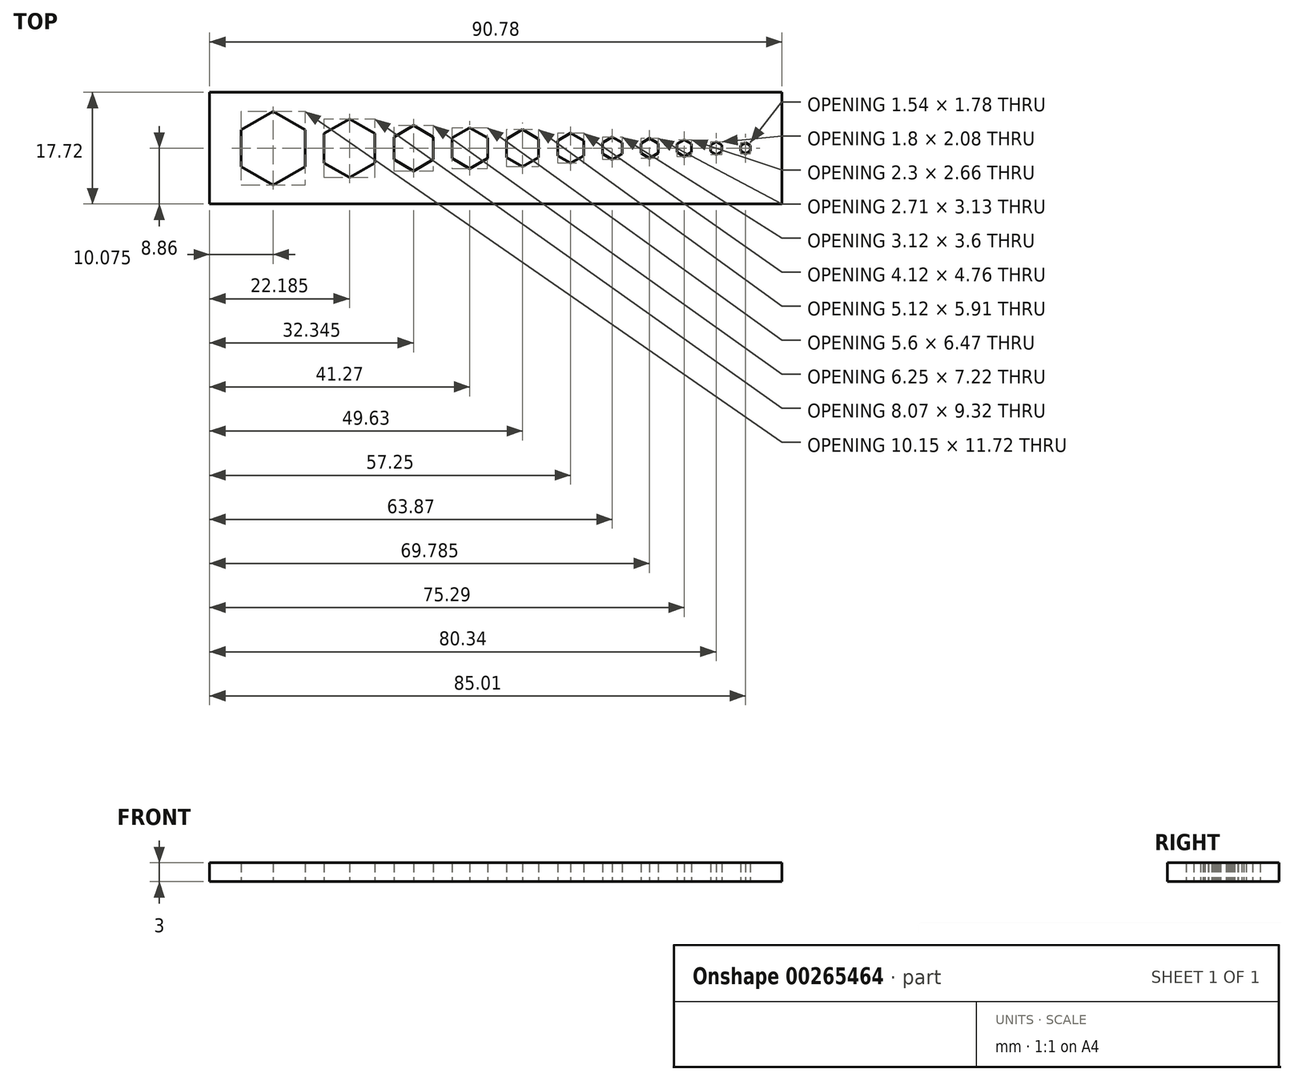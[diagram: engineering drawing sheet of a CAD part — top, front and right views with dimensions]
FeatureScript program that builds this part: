
annotation { "Feature Type Name" : "Feature", "Feature Type Description" : "" }
export const myFeature = defineFeature(function(context is Context, id is Id, definition is map)
    precondition{}
    {
        {
            var Q0;
            Q0=qCreatedBy(makeId("Top.planeOp"),FACE);
            var sketch = newSketch(context, id + "F0", { "sketchPlane" : qUnion([Q0])});
            skCircle(sketch, "E0.cCircle", {"center": v(-42.12, 0) * mm, "radius": 5.07 * mm, "construction": true});
            skLineSegment(sketch, "E0.0", {"start": v(-37.04, 2.93) * mm, "end": v(-37.04, -2.93) * mm});
            skLineSegment(sketch, "E0.1", {"start": v(-37.04, -2.93) * mm, "end": v(-42.12, -5.86) * mm});
            skLineSegment(sketch, "E0.2", {"start": v(-42.12, -5.86) * mm, "end": v(-47.2, -2.93) * mm});
            skLineSegment(sketch, "E0.3", {"start": v(-47.19, -2.93) * mm, "end": v(-47.19, 2.93) * mm});
            skLineSegment(sketch, "E0.4", {"start": v(-47.19, 2.93) * mm, "end": v(-42.11, 5.86) * mm});
            skLineSegment(sketch, "E0.5", {"start": v(-42.11, 5.86) * mm, "end": v(-37.04, 2.93) * mm});
            skPoint(sketch, "E0.0.midPoint", {"position": v(-37.04, 0) * mm});
            skCircle(sketch, "E1.cCircle", {"center": v(-30, 0) * mm, "radius": 4.03 * mm, "construction": true});
            skLineSegment(sketch, "E1.0", {"start": v(-25.97, 2.33) * mm, "end": v(-25.97, -2.33) * mm});
            skLineSegment(sketch, "E1.1", {"start": v(-25.97, -2.33) * mm, "end": v(-30, -4.66) * mm});
            skLineSegment(sketch, "E1.2", {"start": v(-30, -4.66) * mm, "end": v(-34.04, -2.33) * mm});
            skLineSegment(sketch, "E1.3", {"start": v(-34.04, -2.33) * mm, "end": v(-34.04, 2.33) * mm});
            skLineSegment(sketch, "E1.4", {"start": v(-34.04, 2.33) * mm, "end": v(-30, 4.66) * mm});
            skLineSegment(sketch, "E1.5", {"start": v(-30, 4.66) * mm, "end": v(-25.97, 2.33) * mm});
            skPoint(sketch, "E1.0.midPoint", {"position": v(-25.97, 0) * mm});
            skCircle(sketch, "E2.cCircle", {"center": v(-19.85, 0) * mm, "radius": 3.13 * mm, "construction": true});
            skLineSegment(sketch, "E2.0", {"start": v(-16.72, 1.8) * mm, "end": v(-16.72, -1.8) * mm});
            skLineSegment(sketch, "E2.1", {"start": v(-16.72, -1.8) * mm, "end": v(-19.84, -3.6) * mm});
            skLineSegment(sketch, "E2.2", {"start": v(-19.85, -3.6) * mm, "end": v(-22.97, -1.8) * mm});
            skLineSegment(sketch, "E2.3", {"start": v(-22.97, -1.8) * mm, "end": v(-22.97, 1.8) * mm});
            skLineSegment(sketch, "E2.4", {"start": v(-22.97, 1.8) * mm, "end": v(-19.84, 3.6) * mm});
            skLineSegment(sketch, "E2.5", {"start": v(-19.84, 3.6) * mm, "end": v(-16.72, 1.8) * mm});
            skPoint(sketch, "E2.0.midPoint", {"position": v(-16.72, 0) * mm});
            skCircle(sketch, "E3.cCircle", {"center": v(-10.92, 0) * mm, "radius": 2.8 * mm, "construction": true});
            skLineSegment(sketch, "E3.0", {"start": v(-8.12, 1.62) * mm, "end": v(-8.12, -1.62) * mm});
            skLineSegment(sketch, "E3.1", {"start": v(-8.12, -1.62) * mm, "end": v(-10.92, -3.23) * mm});
            skLineSegment(sketch, "E3.2", {"start": v(-10.92, -3.23) * mm, "end": v(-13.72, -1.62) * mm});
            skLineSegment(sketch, "E3.3", {"start": v(-13.72, -1.62) * mm, "end": v(-13.72, 1.62) * mm});
            skLineSegment(sketch, "E3.4", {"start": v(-13.72, 1.62) * mm, "end": v(-10.92, 3.23) * mm});
            skLineSegment(sketch, "E3.5", {"start": v(-10.92, 3.23) * mm, "end": v(-8.12, 1.62) * mm});
            skPoint(sketch, "E3.0.midPoint", {"position": v(-8.12, 0) * mm});
            skCircle(sketch, "E4.cCircle", {"center": v(-2.56, 0) * mm, "radius": 2.56 * mm, "construction": true});
            skLineSegment(sketch, "E4.0", {"start": v(0, 1.48) * mm, "end": v(0, -1.48) * mm});
            skLineSegment(sketch, "E4.1", {"start": v(0, -1.48) * mm, "end": v(-2.56, -2.96) * mm});
            skLineSegment(sketch, "E4.2", {"start": v(-2.56, -2.96) * mm, "end": v(-5.12, -1.48) * mm});
            skLineSegment(sketch, "E4.3", {"start": v(-5.12, -1.48) * mm, "end": v(-5.12, 1.48) * mm});
            skLineSegment(sketch, "E4.4", {"start": v(-5.12, 1.48) * mm, "end": v(-2.56, 2.96) * mm});
            skLineSegment(sketch, "E4.5", {"start": v(-2.56, 2.96) * mm, "end": v(0, 1.48) * mm});
            skPoint(sketch, "E4.0.midPoint", {"position": v(0, 0) * mm});
            skCircle(sketch, "E5.cCircle", {"center": v(5.06, 0) * mm, "radius": 2.06 * mm, "construction": true});
            skLineSegment(sketch, "E5.0", {"start": v(7.12, 1.19) * mm, "end": v(7.12, -1.19) * mm});
            skLineSegment(sketch, "E5.1", {"start": v(7.12, -1.19) * mm, "end": v(5.06, -2.38) * mm});
            skLineSegment(sketch, "E5.2", {"start": v(5.06, -2.38) * mm, "end": v(3, -1.19) * mm});
            skLineSegment(sketch, "E5.3", {"start": v(3, -1.19) * mm, "end": v(3, 1.19) * mm});
            skLineSegment(sketch, "E5.4", {"start": v(3, 1.19) * mm, "end": v(5.06, 2.38) * mm});
            skLineSegment(sketch, "E5.5", {"start": v(5.06, 2.38) * mm, "end": v(7.12, 1.19) * mm});
            skPoint(sketch, "E5.0.midPoint", {"position": v(7.12, 0) * mm});
            skCircle(sketch, "E6.cCircle", {"center": v(11.68, 0) * mm, "radius": 1.56 * mm, "construction": true});
            skLineSegment(sketch, "E6.0", {"start": v(13.24, 0.9) * mm, "end": v(13.24, -0.9) * mm});
            skLineSegment(sketch, "E6.1", {"start": v(13.24, -0.9) * mm, "end": v(11.68, -1.8) * mm});
            skLineSegment(sketch, "E6.2", {"start": v(11.68, -1.8) * mm, "end": v(10.12, -0.9) * mm});
            skLineSegment(sketch, "E6.3", {"start": v(10.12, -0.9) * mm, "end": v(10.12, 0.9) * mm});
            skLineSegment(sketch, "E6.4", {"start": v(10.12, 0.9) * mm, "end": v(11.68, 1.8) * mm});
            skLineSegment(sketch, "E6.5", {"start": v(11.68, 1.8) * mm, "end": v(13.24, 0.9) * mm});
            skPoint(sketch, "E6.0.midPoint", {"position": v(13.24, 0) * mm});
            skCircle(sketch, "E7.cCircle", {"center": v(17.6, 0) * mm, "radius": 1.35 * mm, "construction": true});
            skLineSegment(sketch, "E7.0", {"start": v(18.95, 0.78) * mm, "end": v(18.95, -0.78) * mm});
            skLineSegment(sketch, "E7.1", {"start": v(18.95, -0.78) * mm, "end": v(17.6, -1.56) * mm});
            skLineSegment(sketch, "E7.2", {"start": v(17.6, -1.56) * mm, "end": v(16.24, -0.78) * mm});
            skLineSegment(sketch, "E7.3", {"start": v(16.24, -0.78) * mm, "end": v(16.24, 0.78) * mm});
            skLineSegment(sketch, "E7.4", {"start": v(16.24, 0.78) * mm, "end": v(17.6, 1.56) * mm});
            skLineSegment(sketch, "E7.5", {"start": v(17.6, 1.56) * mm, "end": v(18.95, 0.78) * mm});
            skPoint(sketch, "E7.0.midPoint", {"position": v(18.95, 0) * mm});
            skCircle(sketch, "E8.cCircle", {"center": v(23.1, 0) * mm, "radius": 1.15 * mm, "construction": true});
            skLineSegment(sketch, "E8.0", {"start": v(24.25, 0.66) * mm, "end": v(24.25, -0.66) * mm});
            skLineSegment(sketch, "E8.1", {"start": v(24.25, -0.66) * mm, "end": v(23.1, -1.33) * mm});
            skLineSegment(sketch, "E8.2", {"start": v(23.1, -1.33) * mm, "end": v(21.95, -0.66) * mm});
            skLineSegment(sketch, "E8.3", {"start": v(21.95, -0.66) * mm, "end": v(21.95, 0.66) * mm});
            skLineSegment(sketch, "E8.4", {"start": v(21.95, 0.66) * mm, "end": v(23.1, 1.33) * mm});
            skLineSegment(sketch, "E8.5", {"start": v(23.1, 1.33) * mm, "end": v(24.25, 0.66) * mm});
            skPoint(sketch, "E8.0.midPoint", {"position": v(24.25, 0) * mm});
            skCircle(sketch, "E9.cCircle", {"center": v(28.15, 0) * mm, "radius": 0.9 * mm, "construction": true});
            skLineSegment(sketch, "E9.0", {"start": v(29.05, 0.52) * mm, "end": v(29.05, -0.52) * mm});
            skLineSegment(sketch, "E9.1", {"start": v(29.05, -0.52) * mm, "end": v(28.15, -1.04) * mm});
            skLineSegment(sketch, "E9.2", {"start": v(28.15, -1.04) * mm, "end": v(27.25, -0.52) * mm});
            skLineSegment(sketch, "E9.3", {"start": v(27.25, -0.52) * mm, "end": v(27.25, 0.52) * mm});
            skLineSegment(sketch, "E9.4", {"start": v(27.25, 0.52) * mm, "end": v(28.15, 1.04) * mm});
            skLineSegment(sketch, "E9.5", {"start": v(28.15, 1.04) * mm, "end": v(29.05, 0.52) * mm});
            skPoint(sketch, "E9.0.midPoint", {"position": v(29.05, 0) * mm});
            skCircle(sketch, "E10.cCircle", {"center": v(32.82, 0) * mm, "radius": 0.77 * mm, "construction": true});
            skLineSegment(sketch, "E10.0", {"start": v(33.6, 0.44) * mm, "end": v(33.6, -0.44) * mm});
            skLineSegment(sketch, "E10.1", {"start": v(33.6, -0.44) * mm, "end": v(32.82, -0.89) * mm});
            skLineSegment(sketch, "E10.2", {"start": v(32.82, -0.89) * mm, "end": v(32.05, -0.44) * mm});
            skLineSegment(sketch, "E10.3", {"start": v(32.05, -0.44) * mm, "end": v(32.05, 0.44) * mm});
            skLineSegment(sketch, "E10.4", {"start": v(32.05, 0.44) * mm, "end": v(32.82, 0.89) * mm});
            skLineSegment(sketch, "E10.5", {"start": v(32.82, 0.89) * mm, "end": v(33.6, 0.44) * mm});
            skPoint(sketch, "E10.0.midPoint", {"position": v(33.6, 0) * mm});
            skLineSegment(sketch, "E11.bottom", {"start": v(-52.19, 8.86) * mm, "end": v(38.59, 8.86) * mm});
            skLineSegment(sketch, "E11.top", {"start": v(-52.19, -8.86) * mm, "end": v(38.59, -8.86) * mm});
            skLineSegment(sketch, "E11.left", {"start": v(-52.19, 8.86) * mm, "end": v(-52.19, -8.86) * mm});
            skLineSegment(sketch, "E11.right", {"start": v(38.59, 8.86) * mm, "end": v(38.59, -8.86) * mm});
            skLineSegment(sketch, "E12.left", {"start": v(-52.19, 8.86) * mm, "end": v(-52.19, 8.86) * mm});
            skLineSegment(sketch, "E12.right", {"start": v(38.59, 8.86) * mm, "end": v(38.59, 8.86) * mm});
            skLineSegment(sketch, "E13.top", {"start": v(-52.19, 17.86) * mm, "end": v(38.59, 17.86) * mm});
            skLineSegment(sketch, "E13.left", {"start": v(-52.19, 8.86) * mm, "end": v(-52.19, 17.86) * mm});
            skLineSegment(sketch, "E13.right", {"start": v(38.59, 8.86) * mm, "end": v(38.59, 17.86) * mm});
            skPoint(sketch, "E14", {"position": v(-52.75, 13.36) * mm});
            skPoint(sketch, "E14.positionSnap0", {"position": v(-52.19, 13.36) * mm});
            skPoint(sketch, "E15", {"position": v(39.77, 13.36) * mm});
            skLineSegment(sketch, "E16", {"start": v(-52.75, 13.36) * mm, "end": v(-37.75, 13.36) * mm});
            skLineSegment(sketch, "E17", {"start": v(39.77, 13.36) * mm, "end": v(14.77, 13.36) * mm});
            skLineSegment(sketch, "E18", {"start": v(-19, 13.56) * mm, "end": v(6, 13.56) * mm});
            skSolve(sketch);
        }
        {
            var Q0;
            Q0=makeQuery(id+"F0.imprint","IMPRINT",FACE,{"disambiguationData":[TD([[makeQuery(id+"F0.imprint","IMPRINT",EDGE,{"derivedFrom":sQuery(id+"F0.wireOp",EDGE,"E11.bottom")}),1.0]])]});
            var Q1;
            Q1=makeQuery(id+"F0.imprint","IMPRINT",FACE,{"disambiguationData":[TD([[makeQuery(id+"F0.imprint","IMPRINT",EDGE,{"derivedFrom":sQuery(id+"F0.wireOp",EDGE,"E0.0")}),1.0]])]});
            extrude(context, id + "F1", {"entities" : qUnion([Q0, Q1]), "depth" : 3 * mm});
        }
        {
            var Q0;
            Q0=makeQuery(id+"F1.opExtrude","CAP_FACE",FACE,{"disambiguationData":[OSD([sQuery(id+"F0.wireOp",EDGE,"E0.0"),sQuery(id+"F0.wireOp",EDGE,"E0.1"),sQuery(id+"F0.wireOp",EDGE,"E0.2"),sQuery(id+"F0.wireOp",EDGE,"E0.3"),sQuery(id+"F0.wireOp",EDGE,"E0.4"),sQuery(id+"F0.wireOp",EDGE,"E0.5"),sQuery(id+"F0.wireOp",EDGE,"E1.0"),sQuery(id+"F0.wireOp",EDGE,"E1.1"),sQuery(id+"F0.wireOp",EDGE,"E1.2"),sQuery(id+"F0.wireOp",EDGE,"E1.3"),sQuery(id+"F0.wireOp",EDGE,"E1.4"),sQuery(id+"F0.wireOp",EDGE,"E1.5"),sQuery(id+"F0.wireOp",EDGE,"E2.0"),sQuery(id+"F0.wireOp",EDGE,"E2.1"),sQuery(id+"F0.wireOp",EDGE,"E2.2"),sQuery(id+"F0.wireOp",EDGE,"E2.3"),sQuery(id+"F0.wireOp",EDGE,"E2.4"),sQuery(id+"F0.wireOp",EDGE,"E2.5"),sQuery(id+"F0.wireOp",EDGE,"E3.0"),sQuery(id+"F0.wireOp",EDGE,"E3.1"),sQuery(id+"F0.wireOp",EDGE,"E3.2"),sQuery(id+"F0.wireOp",EDGE,"E3.3"),sQuery(id+"F0.wireOp",EDGE,"E3.4"),sQuery(id+"F0.wireOp",EDGE,"E3.5"),sQuery(id+"F0.wireOp",EDGE,"E4.0"),sQuery(id+"F0.wireOp",EDGE,"E4.1"),sQuery(id+"F0.wireOp",EDGE,"E4.2"),sQuery(id+"F0.wireOp",EDGE,"E4.3"),sQuery(id+"F0.wireOp",EDGE,"E4.4"),sQuery(id+"F0.wireOp",EDGE,"E4.5"),sQuery(id+"F0.wireOp",EDGE,"E5.0"),sQuery(id+"F0.wireOp",EDGE,"E5.1"),sQuery(id+"F0.wireOp",EDGE,"E5.2"),sQuery(id+"F0.wireOp",EDGE,"E5.3"),sQuery(id+"F0.wireOp",EDGE,"E5.4"),sQuery(id+"F0.wireOp",EDGE,"E5.5"),sQuery(id+"F0.wireOp",EDGE,"E6.0"),sQuery(id+"F0.wireOp",EDGE,"E6.1"),sQuery(id+"F0.wireOp",EDGE,"E6.2"),sQuery(id+"F0.wireOp",EDGE,"E6.3"),sQuery(id+"F0.wireOp",EDGE,"E6.4"),sQuery(id+"F0.wireOp",EDGE,"E6.5"),sQuery(id+"F0.wireOp",EDGE,"E7.0"),sQuery(id+"F0.wireOp",EDGE,"E7.1"),sQuery(id+"F0.wireOp",EDGE,"E7.2"),sQuery(id+"F0.wireOp",EDGE,"E7.3"),sQuery(id+"F0.wireOp",EDGE,"E7.4"),sQuery(id+"F0.wireOp",EDGE,"E7.5"),sQuery(id+"F0.wireOp",EDGE,"E8.0"),sQuery(id+"F0.wireOp",EDGE,"E8.1"),sQuery(id+"F0.wireOp",EDGE,"E8.2"),sQuery(id+"F0.wireOp",EDGE,"E8.3"),sQuery(id+"F0.wireOp",EDGE,"E8.4"),sQuery(id+"F0.wireOp",EDGE,"E8.5"),sQuery(id+"F0.wireOp",EDGE,"E9.0"),sQuery(id+"F0.wireOp",EDGE,"E9.1"),sQuery(id+"F0.wireOp",EDGE,"E9.2"),sQuery(id+"F0.wireOp",EDGE,"E9.3"),sQuery(id+"F0.wireOp",EDGE,"E9.4"),sQuery(id+"F0.wireOp",EDGE,"E9.5"),sQuery(id+"F0.wireOp",EDGE,"E10.0"),sQuery(id+"F0.wireOp",EDGE,"E10.1"),sQuery(id+"F0.wireOp",EDGE,"E10.2"),sQuery(id+"F0.wireOp",EDGE,"E10.3"),sQuery(id+"F0.wireOp",EDGE,"E10.4"),sQuery(id+"F0.wireOp",EDGE,"E10.5"),sQuery(id+"F0.wireOp",EDGE,"E11.top"),sQuery(id+"F0.wireOp",EDGE,"E11.left"),sQuery(id+"F0.wireOp",EDGE,"E11.right"),sQuery(id+"F0.wireOp",EDGE,"E13.top"),sQuery(id+"F0.wireOp",EDGE,"E13.left"),sQuery(id+"F0.wireOp",EDGE,"E13.right")])],"isStart":false});
            var sketch = newSketch(context, id + "F2", { "sketchPlane" : qUnion([Q0])});
            skPoint(sketch, "E19", {"position": v(33.59, 13.5) * mm});
            skPoint(sketch, "E20", {"position": v(15.59, 13.5) * mm});
            skPoint(sketch, "E21", {"position": v(2.2, 13.5) * mm});
            skPoint(sketch, "E22", {"position": v(-15.8, 13.5) * mm});
            skPoint(sketch, "E23", {"position": v(-29.19, 13.5) * mm});
            skPoint(sketch, "E24", {"position": v(-47.19, 13.5) * mm});
            skSolve(sketch);
        }
        {
            var Q0;
            Q0=sQuery(id+"F2.wireOp",VERTEX,"E24");
            var Q1;
            Q1=sQuery(id+"F2.wireOp",VERTEX,"E23");
            var Q2;
            Q2=sQuery(id+"F2.wireOp",VERTEX,"E22");
            var Q3;
            Q3=sQuery(id+"F2.wireOp",VERTEX,"E21");
            var Q4;
            Q4=sQuery(id+"F2.wireOp",VERTEX,"E20");
            var Q5;
            Q5=sQuery(id+"F2.wireOp",VERTEX,"E19");
            var Q6;
            Q6=makeQuery(id+"F1.opExtrude","SWEPT_BODY",BODY,{"disambiguationData":[OSD([sQuery(id+"F0.wireOp",EDGE,"E0.0"),sQuery(id+"F0.wireOp",EDGE,"E0.1"),sQuery(id+"F0.wireOp",EDGE,"E0.2"),sQuery(id+"F0.wireOp",EDGE,"E0.3"),sQuery(id+"F0.wireOp",EDGE,"E0.4"),sQuery(id+"F0.wireOp",EDGE,"E0.5"),sQuery(id+"F0.wireOp",EDGE,"E1.0"),sQuery(id+"F0.wireOp",EDGE,"E1.1"),sQuery(id+"F0.wireOp",EDGE,"E1.2"),sQuery(id+"F0.wireOp",EDGE,"E1.3"),sQuery(id+"F0.wireOp",EDGE,"E1.4"),sQuery(id+"F0.wireOp",EDGE,"E1.5"),sQuery(id+"F0.wireOp",EDGE,"E2.0"),sQuery(id+"F0.wireOp",EDGE,"E2.1"),sQuery(id+"F0.wireOp",EDGE,"E2.2"),sQuery(id+"F0.wireOp",EDGE,"E2.3"),sQuery(id+"F0.wireOp",EDGE,"E2.4"),sQuery(id+"F0.wireOp",EDGE,"E2.5"),sQuery(id+"F0.wireOp",EDGE,"E3.0"),sQuery(id+"F0.wireOp",EDGE,"E3.1"),sQuery(id+"F0.wireOp",EDGE,"E3.2"),sQuery(id+"F0.wireOp",EDGE,"E3.3"),sQuery(id+"F0.wireOp",EDGE,"E3.4"),sQuery(id+"F0.wireOp",EDGE,"E3.5"),sQuery(id+"F0.wireOp",EDGE,"E4.0"),sQuery(id+"F0.wireOp",EDGE,"E4.1"),sQuery(id+"F0.wireOp",EDGE,"E4.2"),sQuery(id+"F0.wireOp",EDGE,"E4.3"),sQuery(id+"F0.wireOp",EDGE,"E4.4"),sQuery(id+"F0.wireOp",EDGE,"E4.5"),sQuery(id+"F0.wireOp",EDGE,"E5.0"),sQuery(id+"F0.wireOp",EDGE,"E5.1"),sQuery(id+"F0.wireOp",EDGE,"E5.2"),sQuery(id+"F0.wireOp",EDGE,"E5.3"),sQuery(id+"F0.wireOp",EDGE,"E5.4"),sQuery(id+"F0.wireOp",EDGE,"E5.5"),sQuery(id+"F0.wireOp",EDGE,"E6.0"),sQuery(id+"F0.wireOp",EDGE,"E6.1"),sQuery(id+"F0.wireOp",EDGE,"E6.2"),sQuery(id+"F0.wireOp",EDGE,"E6.3"),sQuery(id+"F0.wireOp",EDGE,"E6.4"),sQuery(id+"F0.wireOp",EDGE,"E6.5"),sQuery(id+"F0.wireOp",EDGE,"E7.0"),sQuery(id+"F0.wireOp",EDGE,"E7.1"),sQuery(id+"F0.wireOp",EDGE,"E7.2"),sQuery(id+"F0.wireOp",EDGE,"E7.3"),sQuery(id+"F0.wireOp",EDGE,"E7.4"),sQuery(id+"F0.wireOp",EDGE,"E7.5"),sQuery(id+"F0.wireOp",EDGE,"E8.0"),sQuery(id+"F0.wireOp",EDGE,"E8.1"),sQuery(id+"F0.wireOp",EDGE,"E8.2"),sQuery(id+"F0.wireOp",EDGE,"E8.3"),sQuery(id+"F0.wireOp",EDGE,"E8.4"),sQuery(id+"F0.wireOp",EDGE,"E8.5"),sQuery(id+"F0.wireOp",EDGE,"E9.0"),sQuery(id+"F0.wireOp",EDGE,"E9.1"),sQuery(id+"F0.wireOp",EDGE,"E9.2"),sQuery(id+"F0.wireOp",EDGE,"E9.3"),sQuery(id+"F0.wireOp",EDGE,"E9.4"),sQuery(id+"F0.wireOp",EDGE,"E9.5"),sQuery(id+"F0.wireOp",EDGE,"E10.0"),sQuery(id+"F0.wireOp",EDGE,"E10.1"),sQuery(id+"F0.wireOp",EDGE,"E10.2"),sQuery(id+"F0.wireOp",EDGE,"E10.3"),sQuery(id+"F0.wireOp",EDGE,"E10.4"),sQuery(id+"F0.wireOp",EDGE,"E10.5"),sQuery(id+"F0.wireOp",EDGE,"E11.top"),sQuery(id+"F0.wireOp",EDGE,"E11.left"),sQuery(id+"F0.wireOp",EDGE,"E11.right"),sQuery(id+"F0.wireOp",EDGE,"E13.top"),sQuery(id+"F0.wireOp",EDGE,"E13.left"),sQuery(id+"F0.wireOp",EDGE,"E13.right")])]});
            hole(context, id + "F3", {"style" : HoleStyle.SIMPLE, "endStyle" : HoleEndStyle.THROUGH, "standardTappedOrClearance" : lookupTablePath({ "standard" : "ISO", "fit" : "Normal", "size" : "M6", "type" : "Clearance" }), "standardBlindInLast" : lookupTablePath({ "fit" : "Standard", "standard" : "ISO", "size" : "M6", "type" : "Clearance" }), "holeDiameter" : 6.6 * mm, "tappedDepth" : 12 * mm, "tapClearance" : 3, "locations" : qUnion([Q0, Q1, Q2, Q3, Q4, Q5]), "scope" : qUnion([Q6])});
        }
        {
            var Q0;
            Q0=makeQuery(id+"F1.opExtrude","CAP_FACE",FACE,{"disambiguationData":[OSD([sQuery(id+"F0.wireOp",EDGE,"E0.0"),sQuery(id+"F0.wireOp",EDGE,"E0.1"),sQuery(id+"F0.wireOp",EDGE,"E0.2"),sQuery(id+"F0.wireOp",EDGE,"E0.3"),sQuery(id+"F0.wireOp",EDGE,"E0.4"),sQuery(id+"F0.wireOp",EDGE,"E0.5"),sQuery(id+"F0.wireOp",EDGE,"E1.0"),sQuery(id+"F0.wireOp",EDGE,"E1.1"),sQuery(id+"F0.wireOp",EDGE,"E1.2"),sQuery(id+"F0.wireOp",EDGE,"E1.3"),sQuery(id+"F0.wireOp",EDGE,"E1.4"),sQuery(id+"F0.wireOp",EDGE,"E1.5"),sQuery(id+"F0.wireOp",EDGE,"E2.0"),sQuery(id+"F0.wireOp",EDGE,"E2.1"),sQuery(id+"F0.wireOp",EDGE,"E2.2"),sQuery(id+"F0.wireOp",EDGE,"E2.3"),sQuery(id+"F0.wireOp",EDGE,"E2.4"),sQuery(id+"F0.wireOp",EDGE,"E2.5"),sQuery(id+"F0.wireOp",EDGE,"E3.0"),sQuery(id+"F0.wireOp",EDGE,"E3.1"),sQuery(id+"F0.wireOp",EDGE,"E3.2"),sQuery(id+"F0.wireOp",EDGE,"E3.3"),sQuery(id+"F0.wireOp",EDGE,"E3.4"),sQuery(id+"F0.wireOp",EDGE,"E3.5"),sQuery(id+"F0.wireOp",EDGE,"E4.0"),sQuery(id+"F0.wireOp",EDGE,"E4.1"),sQuery(id+"F0.wireOp",EDGE,"E4.2"),sQuery(id+"F0.wireOp",EDGE,"E4.3"),sQuery(id+"F0.wireOp",EDGE,"E4.4"),sQuery(id+"F0.wireOp",EDGE,"E4.5"),sQuery(id+"F0.wireOp",EDGE,"E5.0"),sQuery(id+"F0.wireOp",EDGE,"E5.1"),sQuery(id+"F0.wireOp",EDGE,"E5.2"),sQuery(id+"F0.wireOp",EDGE,"E5.3"),sQuery(id+"F0.wireOp",EDGE,"E5.4"),sQuery(id+"F0.wireOp",EDGE,"E5.5"),sQuery(id+"F0.wireOp",EDGE,"E6.0"),sQuery(id+"F0.wireOp",EDGE,"E6.1"),sQuery(id+"F0.wireOp",EDGE,"E6.2"),sQuery(id+"F0.wireOp",EDGE,"E6.3"),sQuery(id+"F0.wireOp",EDGE,"E6.4"),sQuery(id+"F0.wireOp",EDGE,"E6.5"),sQuery(id+"F0.wireOp",EDGE,"E7.0"),sQuery(id+"F0.wireOp",EDGE,"E7.1"),sQuery(id+"F0.wireOp",EDGE,"E7.2"),sQuery(id+"F0.wireOp",EDGE,"E7.3"),sQuery(id+"F0.wireOp",EDGE,"E7.4"),sQuery(id+"F0.wireOp",EDGE,"E7.5"),sQuery(id+"F0.wireOp",EDGE,"E8.0"),sQuery(id+"F0.wireOp",EDGE,"E8.1"),sQuery(id+"F0.wireOp",EDGE,"E8.2"),sQuery(id+"F0.wireOp",EDGE,"E8.3"),sQuery(id+"F0.wireOp",EDGE,"E8.4"),sQuery(id+"F0.wireOp",EDGE,"E8.5"),sQuery(id+"F0.wireOp",EDGE,"E9.0"),sQuery(id+"F0.wireOp",EDGE,"E9.1"),sQuery(id+"F0.wireOp",EDGE,"E9.2"),sQuery(id+"F0.wireOp",EDGE,"E9.3"),sQuery(id+"F0.wireOp",EDGE,"E9.4"),sQuery(id+"F0.wireOp",EDGE,"E9.5"),sQuery(id+"F0.wireOp",EDGE,"E10.0"),sQuery(id+"F0.wireOp",EDGE,"E10.1"),sQuery(id+"F0.wireOp",EDGE,"E10.2"),sQuery(id+"F0.wireOp",EDGE,"E10.3"),sQuery(id+"F0.wireOp",EDGE,"E10.4"),sQuery(id+"F0.wireOp",EDGE,"E10.5"),sQuery(id+"F0.wireOp",EDGE,"E11.top"),sQuery(id+"F0.wireOp",EDGE,"E11.left"),sQuery(id+"F0.wireOp",EDGE,"E11.right"),sQuery(id+"F0.wireOp",EDGE,"E13.top"),sQuery(id+"F0.wireOp",EDGE,"E13.left"),sQuery(id+"F0.wireOp",EDGE,"E13.right")])],"isStart":false});
            var sketch = newSketch(context, id + "F4", { "sketchPlane" : qUnion([Q0])});
            skLineSegment(sketch, "E25", {"start": v(-47.27, 16.8) * mm, "end": v(-29.2, 16.8) * mm});
            skLineSegment(sketch, "E26", {"start": v(-29.2, 16.8) * mm, "end": v(-29.2, 10.2) * mm});
            skLineSegment(sketch, "E27", {"start": v(-29.2, 10.2) * mm, "end": v(-47.1, 10.2) * mm});
            skLineSegment(sketch, "E28", {"start": v(-47.1, 10.2) * mm, "end": v(-47.27, 16.8) * mm});
            skLineSegment(sketch, "E29", {"start": v(-15.88, 16.8) * mm, "end": v(-15.88, 10.2) * mm});
            skLineSegment(sketch, "E30", {"start": v(-15.88, 10.2) * mm, "end": v(2.2, 10.2) * mm});
            skLineSegment(sketch, "E31", {"start": v(2.2, 10.2) * mm, "end": v(2.2, 16.8) * mm});
            skLineSegment(sketch, "E32", {"start": v(2.2, 16.8) * mm, "end": v(-15.88, 16.8) * mm});
            skLineSegment(sketch, "E33", {"start": v(15.5, 16.8) * mm, "end": v(15.5, 10.2) * mm});
            skLineSegment(sketch, "E34", {"start": v(15.5, 10.2) * mm, "end": v(33.7, 10.2) * mm});
            skLineSegment(sketch, "E35", {"start": v(33.7, 10.2) * mm, "end": v(33.7, 16.8) * mm});
            skLineSegment(sketch, "E36", {"start": v(33.7, 16.8) * mm, "end": v(15.5, 16.8) * mm});
            skSolve(sketch);
        }
        {
            var Q0;
            {var subQ6=sQuery(id+"F4.wireOp",EDGE,"E27");Q0=makeQuery(id+"F4.imprint","IMPRINT",FACE,{"disambiguationData":[TD([[makeQuery(id+"F4.imprint","IMPRINT",EDGE,{"derivedFrom":subQ6}),-1.0]])]});}
            var Q1;
            {var subQ1=sQuery(id+"F4.wireOp",EDGE,"E30");var subQ4=makeQuery(id+"F3.hole-2.boolean.opBoolean","COPY",EDGE,{"derivedFrom":makeQuery(id+"F3.hole-2.opRevolve","SWEPT_EDGE",EDGE,{"disambiguationData":[OSD([sQuery(id+"F3.hole-2.sketch.wireOp",EDGE,"core_line_2"),sQuery(id+"F3.hole-2.sketch.wireOp",EDGE,"core_line_3")])]})});var subQ5=makeQuery(id+"F4.imprint","INTERSECT",VERTEX,{"derivedFrom":[subQ4,subQ1]});Q1=makeQuery(id+"F4.imprint","IMPRINT",FACE,{"disambiguationData":[TD([[makeQuery(id+"F4.imprint","IMPRINT",EDGE,{"disambiguationData":[TD([[subQ5,-1.0]])],"derivedFrom":subQ1}),1.0]])]});}
            var Q2;
            {var subQ0=sQuery(id+"F4.wireOp",EDGE,"E34");var subQ1=makeQuery(id+"F3.hole-4.boolean.opBoolean","COPY",EDGE,{"derivedFrom":makeQuery(id+"F3.hole-4.opRevolve","SWEPT_EDGE",EDGE,{"disambiguationData":[OSD([sQuery(id+"F3.hole-4.sketch.wireOp",EDGE,"core_line_2"),sQuery(id+"F3.hole-4.sketch.wireOp",EDGE,"core_line_3")])]})});var subQ2=makeQuery(id+"F4.imprint","INTERSECT",VERTEX,{"derivedFrom":[subQ1,subQ0]});Q2=makeQuery(id+"F4.imprint","IMPRINT",FACE,{"disambiguationData":[TD([[makeQuery(id+"F4.imprint","IMPRINT",EDGE,{"disambiguationData":[TD([[subQ2,-1.0]])],"derivedFrom":subQ0}),1.0]])]});}
            extrude(context, id + "F5", {"entities" : qUnion([Q0, Q1, Q2]), "operationType" : NewBodyOperationType.REMOVE, "oppositeDirection" : true, "depth" : 25 * mm});
        }
    });
